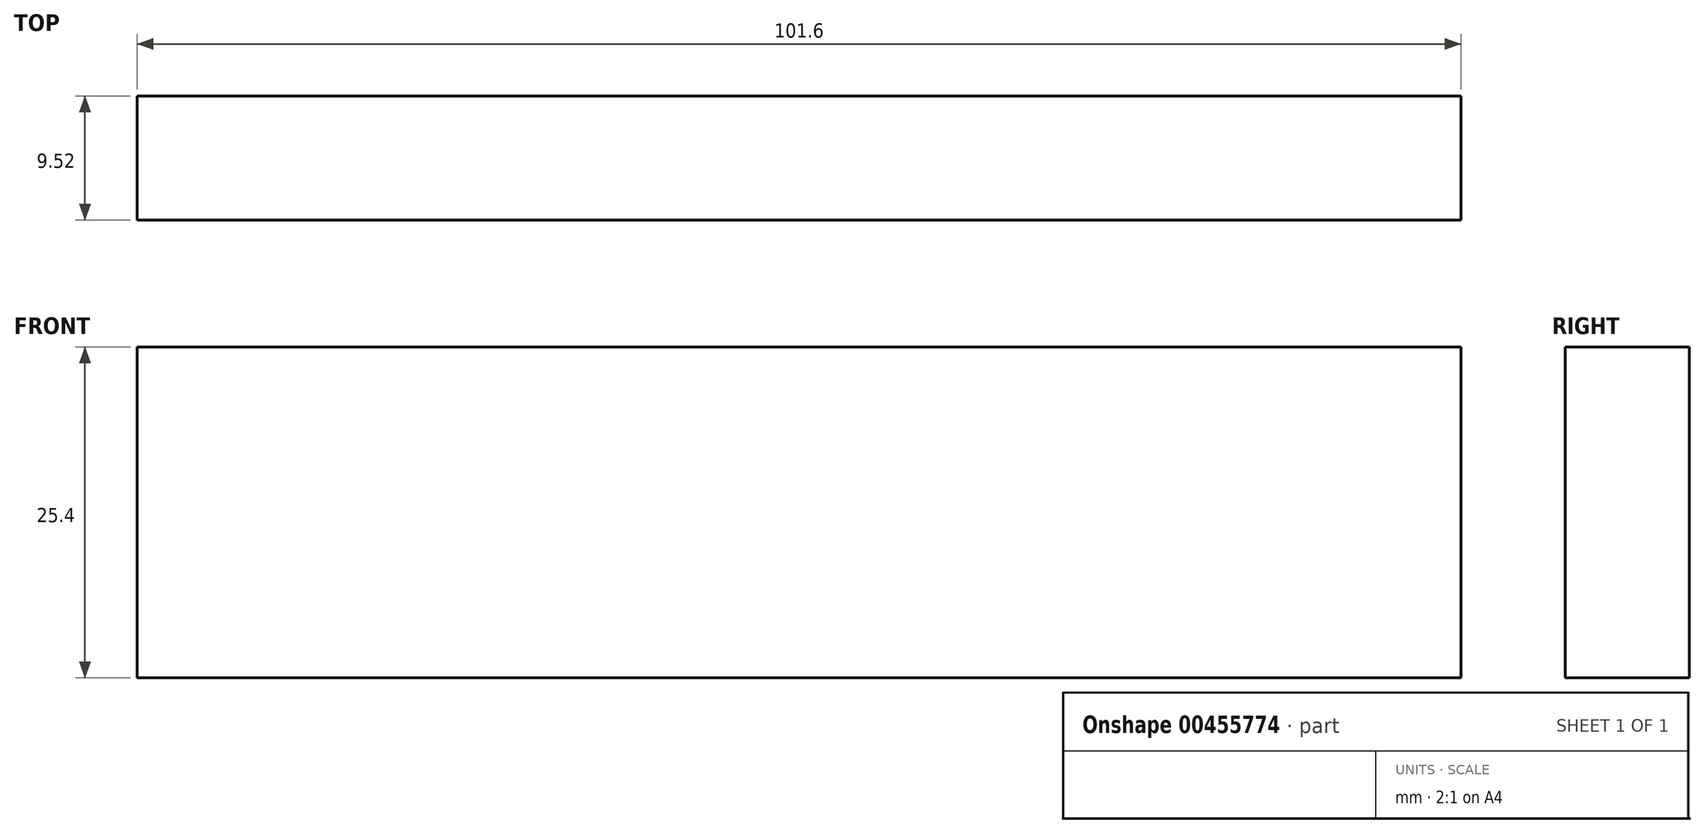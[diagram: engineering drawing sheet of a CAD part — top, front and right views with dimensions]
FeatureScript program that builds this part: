
annotation { "Feature Type Name" : "Feature", "Feature Type Description" : "" }
export const myFeature = defineFeature(function(context is Context, id is Id, definition is map)
    precondition{}
    {
        {
            var Q0;
            Q0=qCreatedBy(makeId("Top.planeOp"),FACE);
            var sketch = newSketch(context, id + "F0", { "sketchPlane" : qUnion([Q0])});
            skLineSegment(sketch, "E0.bottom", {"start": v(-47.51, -194.23) * mm, "end": v(54.09, -194.23) * mm});
            skLineSegment(sketch, "E0.top", {"start": v(-47.51, -203.75) * mm, "end": v(54.09, -203.75) * mm});
            skLineSegment(sketch, "E0.left", {"start": v(-47.51, -194.23) * mm, "end": v(-47.51, -203.75) * mm});
            skLineSegment(sketch, "E0.right", {"start": v(54.09, -194.23) * mm, "end": v(54.09, -203.75) * mm});
            skSolve(sketch);
        }
        {
            var Q0;
            Q0 = qSketchRegion(id + "F0", true);
            extrude(context, id + "F1", {"entities" : qUnion([Q0]), "oppositeDirection" : true, "depth" : 25.4 * mm});
        }
    });
